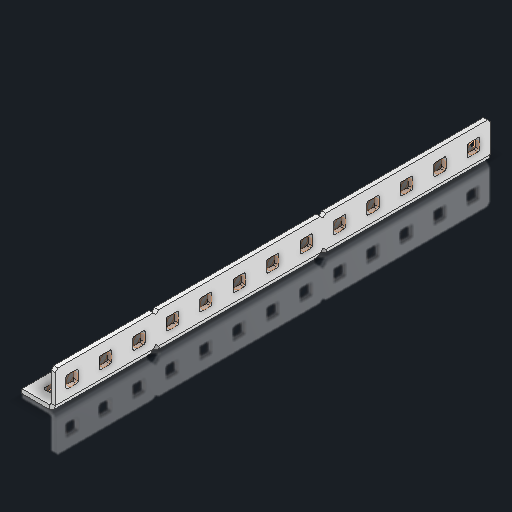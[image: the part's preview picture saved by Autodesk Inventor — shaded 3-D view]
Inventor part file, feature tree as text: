
AUTODESK INVENTOR PART (.ipt)
format: ipt  version: 2023.2 (Build 272271030, 271C)  size: 586,752 bytes
history: native  units: in
note: dims shown in document units (in); Inventor stores cm internally (conversion verified against a paired STEP export)
features: other x58, sketch x8, sheet_metal_op x1
ambient origin geometry x8: Origin, YZ Plane, XZ Plane, XY Plane, X Axis, Y Axis, Z Axis, Center Point
bodies: Solid1 (feature_tree)
feature tree (67):
  other  "Alu C Half 1x3x1x13.ipt"
  other  "Solid1::Alu C Half 1x3x1x13.ipt"
  other  "TaggingFeature1"
  sketch  "Sketch1"  dims[d0=0.3937in]
  sketch  "Sketch2"  dims[d1=0.0625in]
  sketch  "Sketch3"
  sketch  "Sketch7"
  other  "Flange Pattern Sketch"
  sketch  "Sketch8"
  sketch  "Sketch9"
  sheet_metal_op  "Body Pattern Sketch"
  other  "Arc Length"
  sketch  "Sketch13"
  sketch  "Sketch14"
  other  "Flange Pattern Plane"
  other  "Srf1"
  other  "Srf2"
  other  "Srf3"
  other  "Srf4"
  other  "Srf5"
  other  "Srf6"
  other  "Srf7"
  other  "Srf8"
  other  "Srf9"
  other  "Srf10"
  other  "Srf11"
  other  "Srf12"
  other  "Srf13"
  other  "Srf14"
  other  "Srf15"
  other  "Srf16"
  other  "Srf17"
  other  "Srf18"
  other  "Srf19"
  other  "Srf20"
  other  "Srf21"
  other  "Srf22"
  other  "Srf23"
  other  "Srf24"
  other  "Srf25"
  other  "Srf26"
  other  "Srf1::Derived"
  other  "Srf2::Derived"
  other  "Srf1310::Derived"
  other  "Srf1311::Derived"
  other  "Srf1312::Derived"
  other  "Srf1728::Derived"
  other  "Srf1878::Derived"
  other  "Srf1879::Derived"
  other  "Srf1880::Derived"
  other  "Srf1881::Derived"
  other  "Srf1882::Derived"
  other  "Srf1883::Derived"
  other  "Srf1884::Derived"
  other  "Srf91::Derived"
  other  "Srf92::Derived"
  other  "Srf856::Derived"
  other  "Srf1376::Derived"
  other  "Srf1377::Derived"
  other  "Srf1755::Derived"
  other  "Srf1942::Derived"
  other  "Srf1943::Derived"
  other  "Srf1944::Derived"
  other  "Srf1945::Derived"
  other  "Srf1946::Derived"
  other  "Srf1947::Derived"
  other  "Srf1948::Derived"
